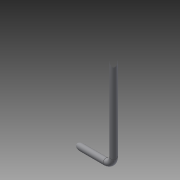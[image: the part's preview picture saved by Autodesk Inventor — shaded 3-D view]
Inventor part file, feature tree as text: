
AUTODESK INVENTOR PART (.ipt)
format: ipt  version: 2014 SP1 (Build 180222100, 222)  size: 79,872 bytes
history: native  units: in
note: dims shown in document units (in); Inventor stores cm internally (conversion verified against a paired STEP export)
features: sketch x2, sweep x1
ambient origin geometry x8: Origin, YZ Plane, XZ Plane, XY Plane, X Axis, Y Axis, Z Axis, Center Point
bodies: Solid1 (feature_tree)
feature tree (3):
  sweep  "Sweep1"
  sketch  "Sketch1"  dims[d3=0.3in d4=0.0in]
  sketch  "Sketch2"  dims[d5=5.5in d6=0.375in]
